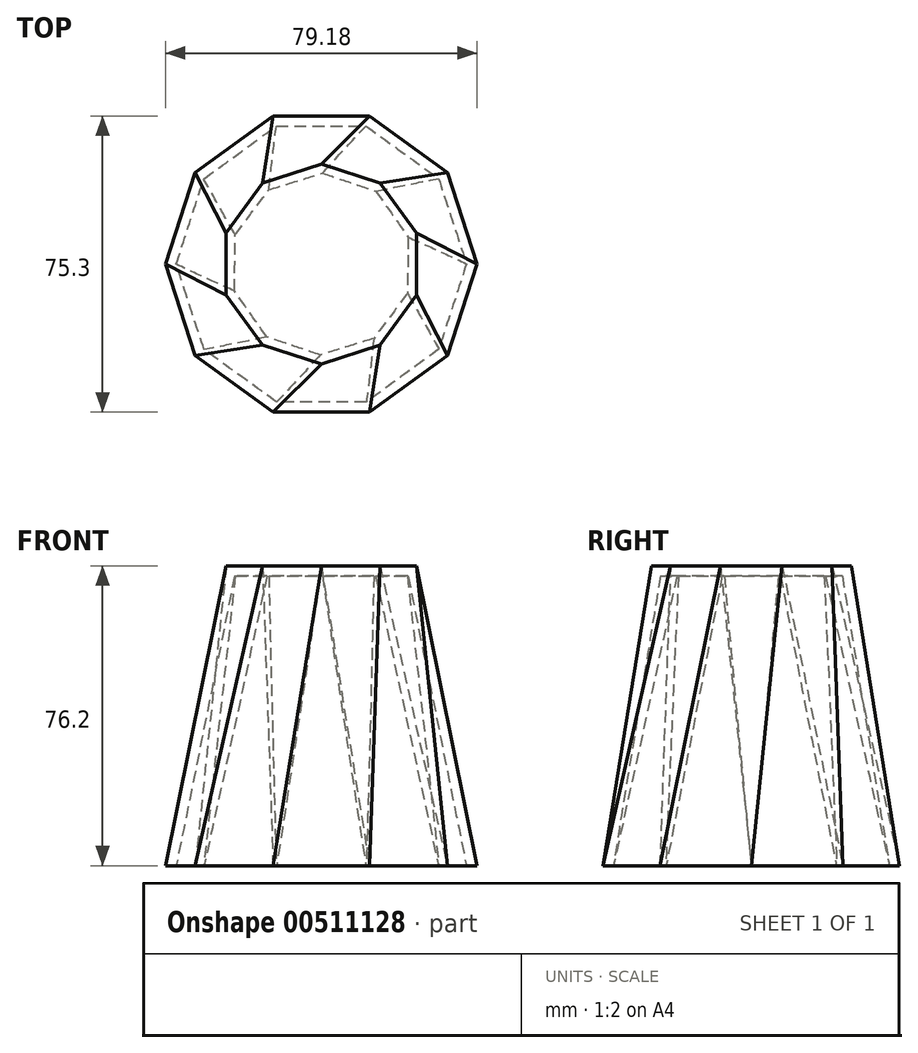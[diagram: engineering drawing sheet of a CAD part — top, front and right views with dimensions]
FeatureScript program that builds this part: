
annotation { "Feature Type Name" : "Feature", "Feature Type Description" : "" }
export const myFeature = defineFeature(function(context is Context, id is Id, definition is map)
    precondition{}
    {
        {
            var Q0;
            Q0=qCreatedBy(makeId("Top.planeOp"),FACE);
            var sketch = newSketch(context, id + "F0", { "sketchPlane" : qUnion([Q0])});
            skCircle(sketch, "E0.cCircle", {"center": v(0, 0) * mm, "radius": 39.59 * mm, "construction": true});
            skLineSegment(sketch, "E0.0", {"start": v(12.23, -37.65) * mm, "end": v(-12.23, -37.65) * mm});
            skLineSegment(sketch, "E0.1", {"start": v(-12.23, -37.65) * mm, "end": v(-32.03, -23.27) * mm});
            skLineSegment(sketch, "E0.2", {"start": v(-32.03, -23.27) * mm, "end": v(-39.59, 0) * mm});
            skLineSegment(sketch, "E0.3", {"start": v(-39.59, 0) * mm, "end": v(-32.03, 23.27) * mm});
            skLineSegment(sketch, "E0.4", {"start": v(-32.03, 23.27) * mm, "end": v(-12.23, 37.65) * mm});
            skLineSegment(sketch, "E0.5", {"start": v(-12.23, 37.65) * mm, "end": v(12.23, 37.65) * mm});
            skLineSegment(sketch, "E0.6", {"start": v(12.23, 37.65) * mm, "end": v(32.03, 23.27) * mm});
            skLineSegment(sketch, "E0.7", {"start": v(32.03, 23.27) * mm, "end": v(39.59, 0) * mm});
            skLineSegment(sketch, "E0.8", {"start": v(39.59, 0) * mm, "end": v(32.03, -23.27) * mm});
            skLineSegment(sketch, "E0.9", {"start": v(32.03, -23.27) * mm, "end": v(12.23, -37.65) * mm});
            skSolve(sketch);
        }
        {
            var Q0;
            Q0=qCreatedBy(makeId("Top.planeOp"),FACE);
            cPlane(context, id + "F1", {"entities" : qUnion([Q0]), "cplaneType" : CPlaneType.OFFSET, "offset" : 76.2 * mm, "width" : 152.4 * mm, "height" : 152.4 * mm});
        }
        {
            var Q0;
            Q0=qCreatedBy(id+"F1.planeOp",FACE);
            var sketch = newSketch(context, id + "F2", { "sketchPlane" : qUnion([Q0])});
            skCircle(sketch, "E1.cCircle", {"center": v(0, 0) * mm, "radius": 25.4 * mm, "construction": true});
            skLineSegment(sketch, "E1.0", {"start": v(14.93, -20.55) * mm, "end": v(0, -25.4) * mm});
            skLineSegment(sketch, "E1.1", {"start": v(0, -25.4) * mm, "end": v(-14.93, -20.55) * mm});
            skLineSegment(sketch, "E1.2", {"start": v(-14.93, -20.55) * mm, "end": v(-24.16, -7.85) * mm});
            skLineSegment(sketch, "E1.3", {"start": v(-24.16, -7.85) * mm, "end": v(-24.16, 7.85) * mm});
            skLineSegment(sketch, "E1.4", {"start": v(-24.16, 7.85) * mm, "end": v(-14.93, 20.55) * mm});
            skLineSegment(sketch, "E1.5", {"start": v(-14.93, 20.55) * mm, "end": v(0, 25.4) * mm});
            skLineSegment(sketch, "E1.6", {"start": v(0, 25.4) * mm, "end": v(14.93, 20.55) * mm});
            skLineSegment(sketch, "E1.7", {"start": v(14.93, 20.55) * mm, "end": v(24.16, 7.85) * mm});
            skLineSegment(sketch, "E1.8", {"start": v(24.16, 7.85) * mm, "end": v(24.16, -7.85) * mm});
            skLineSegment(sketch, "E1.9", {"start": v(24.16, -7.85) * mm, "end": v(14.93, -20.55) * mm});
            skSolve(sketch);
        }
        {
            var Q0;
            Q0=makeQuery(id+"F2.imprint","IMPRINT",FACE,{"disambiguationData":[TD([[makeQuery(id+"F2.imprint","IMPRINT",EDGE,{"derivedFrom":sQuery(id+"F2.wireOp",EDGE,"E1.0")}),-1.0]])]});
            var Q1;
            Q1=makeQuery(id+"F0.imprint","IMPRINT",FACE,{"disambiguationData":[TD([[makeQuery(id+"F0.imprint","IMPRINT",EDGE,{"derivedFrom":sQuery(id+"F0.wireOp",EDGE,"E0.0")}),-1.0]])]});
            loft(context, id + "F3", {"sheetProfilesArray" : [{ "sheetProfileEntities" : qUnion([Q0]) }, { "sheetProfileEntities" : qUnion([Q1]) }]});
        }
        {
            var Q0;
            Q0=makeQuery(id+"F3.opLoft","CAP_FACE",FACE,{"disambiguationData":[OSD([makeQuery(id+"F0.imprint","IMPRINT",FACE,{"disambiguationData":[TD([[makeQuery(id+"F0.imprint","IMPRINT",EDGE,{"derivedFrom":sQuery(id+"F0.wireOp",EDGE,"E0.0")}),-1.0]])]})])],"isStart":true});
            shell(context, id + "F4", {"entities" : qUnion([Q0]), "thickness" : 2.54 * mm});
        }
    });
